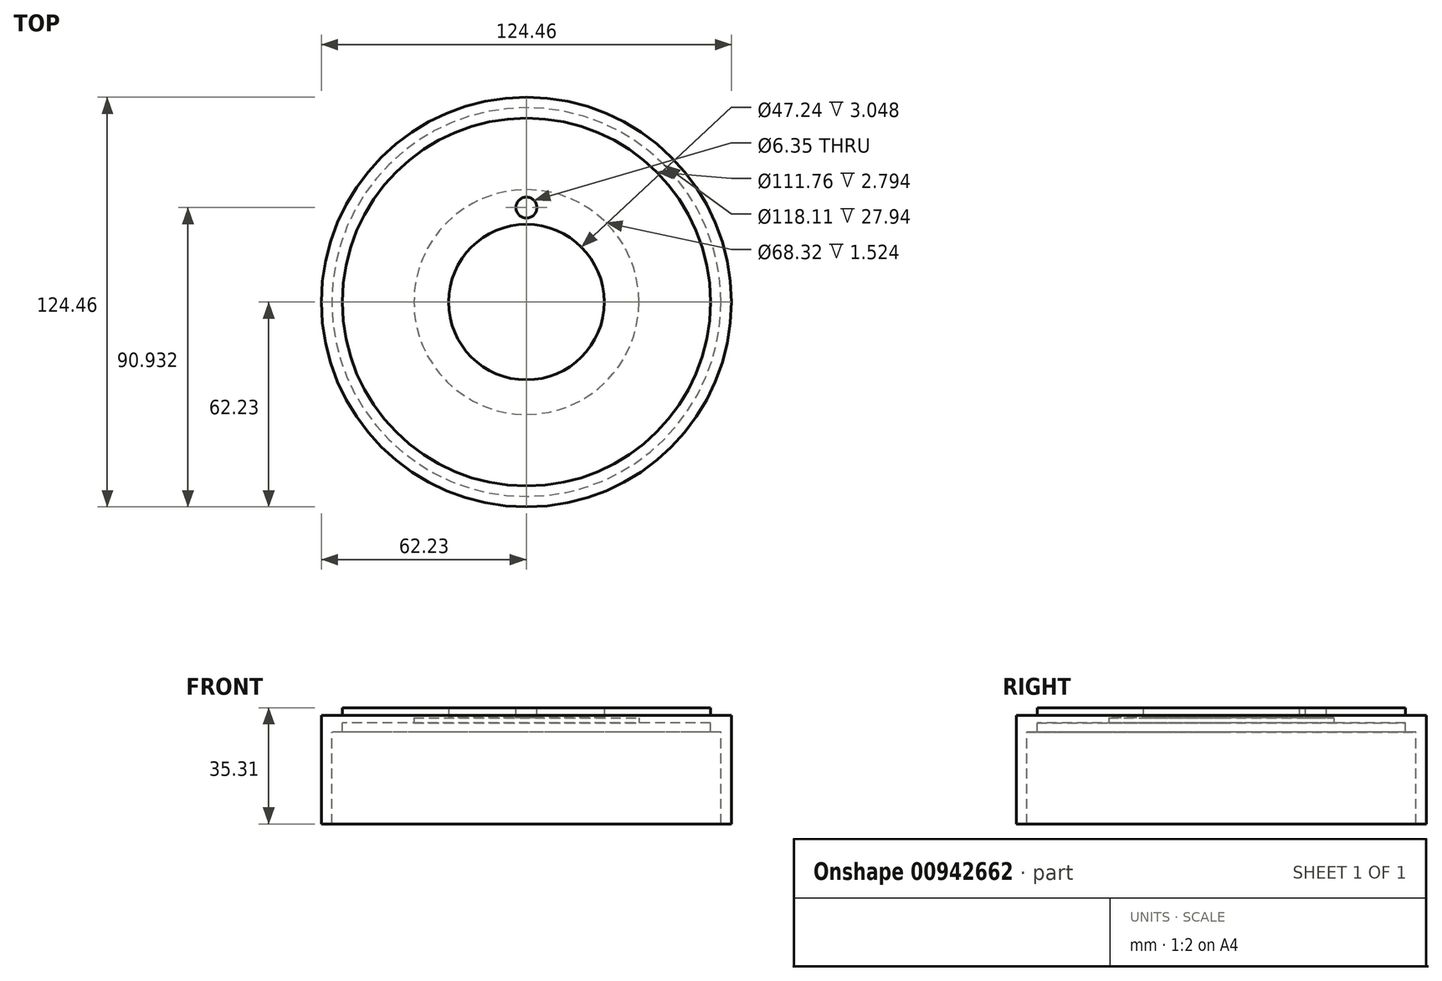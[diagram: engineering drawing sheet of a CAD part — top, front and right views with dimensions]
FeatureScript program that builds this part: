
annotation { "Feature Type Name" : "Feature", "Feature Type Description" : "" }
export const myFeature = defineFeature(function(context is Context, id is Id, definition is map)
    precondition{}
    {
        {
            var Q0;
            Q0=qCreatedBy(makeId("Top.planeOp"),FACE);
            var sketch = newSketch(context, id + "F0", { "sketchPlane" : qUnion([Q0])});
            skCircle(sketch, "E0", {"center": v(0, 0) * mm, "radius": 59.06 * mm});
            skCircle(sketch, "E1", {"center": v(0, 0) * mm, "radius": 55.88 * mm});
            skCircle(sketch, "E2", {"center": v(0, 0) * mm, "radius": 62.23 * mm});
            skCircle(sketch, "E3", {"center": v(0, 0) * mm, "radius": 23.62 * mm});
            skSolve(sketch);
        }
        {
            var Q0;
            Q0=makeQuery(id+"F0.imprint","IMPRINT",FACE,{"disambiguationData":[TD([[makeQuery(id+"F0.imprint","IMPRINT",EDGE,{"derivedFrom":sQuery(id+"F0.wireOp",EDGE,"E1")}),1.0]])]});
            extrude(context, id + "F1", {"entities" : qUnion([Q0]), "endBound" : BoundingType.SYMMETRIC, "depth" : 4.57 * mm, "offsetDistance" : 25.4 * mm});
        }
        {
            var Q0;
            Q0=makeQuery(id+"F0.imprint","IMPRINT",FACE,{"disambiguationData":[TD([[makeQuery(id+"F0.imprint","IMPRINT",EDGE,{"derivedFrom":sQuery(id+"F0.wireOp",EDGE,"E0")}),1.0]])]});
            extrude(context, id + "F2", {"entities" : qUnion([Q0]), "operationType" : NewBodyOperationType.ADD, "oppositeDirection" : true, "depth" : 5.08 * mm, "offsetDistance" : 25.4 * mm});
        }
        {
            var Q0;
            Q0=makeQuery(id+"F0.imprint","IMPRINT",FACE,{"disambiguationData":[TD([[makeQuery(id+"F0.imprint","IMPRINT",EDGE,{"derivedFrom":sQuery(id+"F0.wireOp",EDGE,"E0")}),-1.0]])]});
            extrude(context, id + "F3", {"entities" : qUnion([Q0]), "operationType" : NewBodyOperationType.ADD, "oppositeDirection" : true, "depth" : 33.02 * mm, "offsetDistance" : 25.4 * mm});
        }
        {
            var Q0;
            Q0=makeQuery(id+"F1.opExtrude","CAP_FACE",FACE,{"disambiguationData":[OSD([sQuery(id+"F0.wireOp",EDGE,"E1"),sQuery(id+"F0.wireOp",EDGE,"E3")])],"isStart":false});
            var sketch = newSketch(context, id + "F4", { "sketchPlane" : qUnion([Q0])});
            skCircle(sketch, "E4", {"center": v(0, 28.7) * mm, "radius": 3.18 * mm});
            skSolve(sketch);
        }
        {
            var Q0;
            Q0=makeQuery(id+"F4.imprint","IMPRINT",FACE,{"disambiguationData":[TD([[makeQuery(id+"F4.imprint","IMPRINT",EDGE,{"derivedFrom":sQuery(id+"F4.wireOp",EDGE,"E4")}),1.0]])]});
            extrude(context, id + "F5", {"entities" : qUnion([Q0]), "operationType" : NewBodyOperationType.REMOVE, "oppositeDirection" : true, "depth" : 25.4 * mm, "offsetDistance" : 25.4 * mm});
        }
        {
            var Q0;
            Q0=qCreatedBy(makeId("Front.planeOp"),FACE);
            var sketch = newSketch(context, id + "F6", { "sketchPlane" : qUnion([Q0])});
            skLineSegment(sketch, "E5", {"start": v(0, -48.63) * mm, "end": v(0, 24.12) * mm, "construction": true});
            skSolve(sketch);
        }
        {
            var Q0;
            Q0=makeQuery(id+"F1.opExtrude","CAP_FACE",FACE,{"disambiguationData":[OSD([sQuery(id+"F0.wireOp",EDGE,"E1"),sQuery(id+"F0.wireOp",EDGE,"E3")])],"isStart":true});
            var sketch = newSketch(context, id + "F7", { "sketchPlane" : qUnion([Q0])});
            skCircle(sketch, "E6", {"center": v(0, 0) * mm, "radius": 34.16 * mm});
            skSolve(sketch);
        }
        {
            var Q0;
            Q0=makeQuery(id+"F7.imprint","IMPRINT",FACE,{"disambiguationData":[TD([[makeQuery(id+"F7.imprint","IMPRINT",EDGE,{"derivedFrom":sQuery(id+"F7.wireOp",EDGE,"E6")}),1.0]])]});
            extrude(context, id + "F8", {"entities" : qUnion([Q0]), "operationType" : NewBodyOperationType.REMOVE, "oppositeDirection" : true, "depth" : 1.52 * mm, "offsetDistance" : 25.4 * mm});
        }
    });
